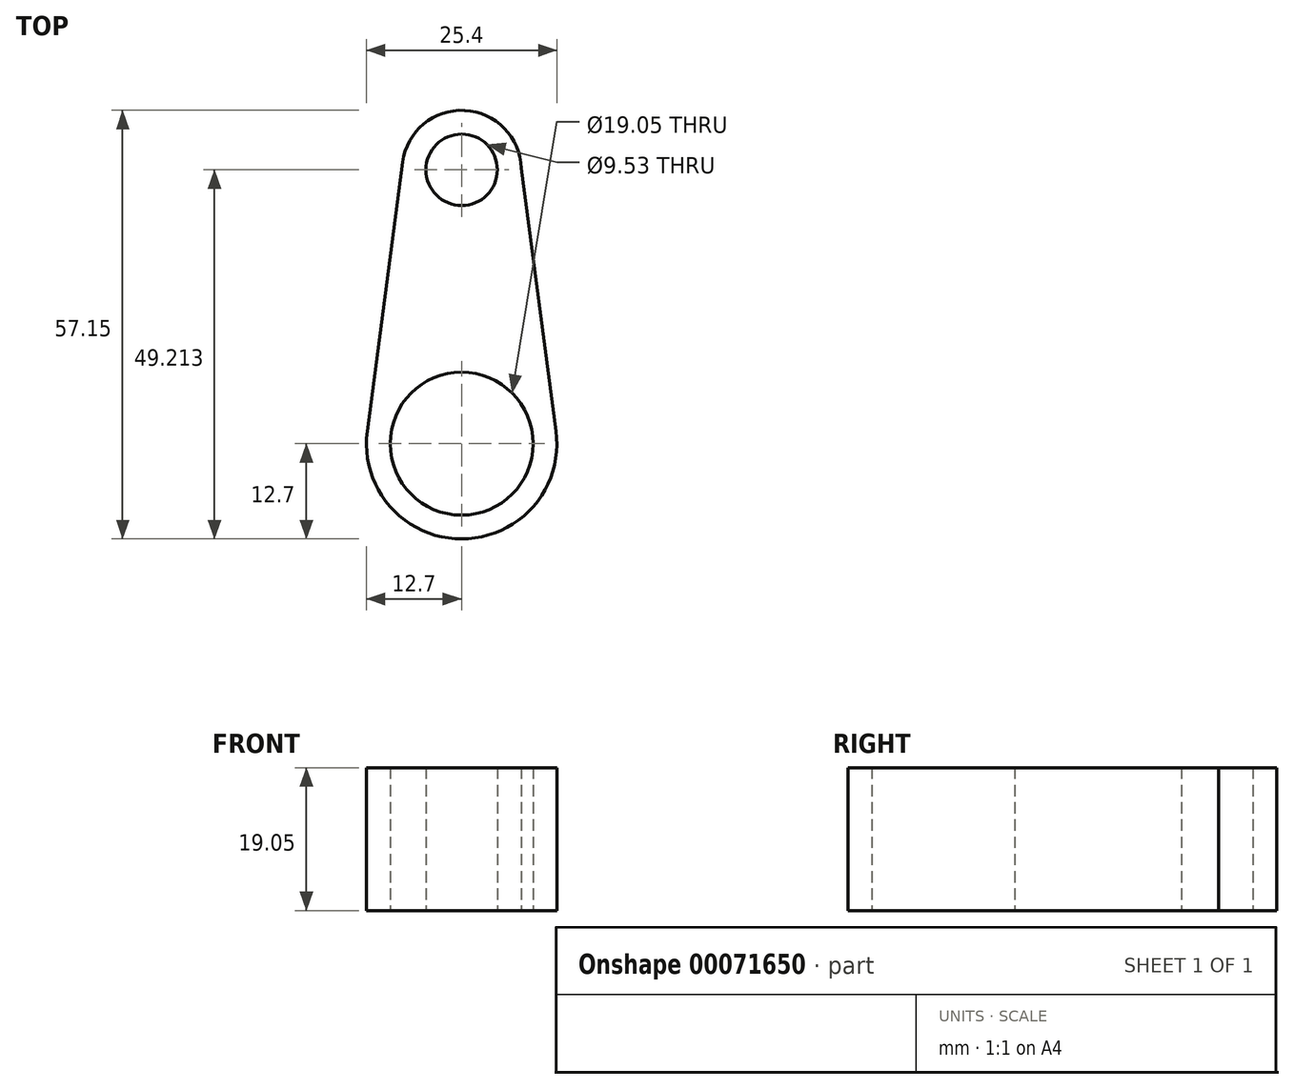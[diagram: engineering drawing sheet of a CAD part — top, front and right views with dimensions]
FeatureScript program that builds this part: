
annotation { "Feature Type Name" : "Feature", "Feature Type Description" : "" }
export const myFeature = defineFeature(function(context is Context, id is Id, definition is map)
    precondition{}
    {
        {
            var Q0;
            Q0=qCreatedBy(makeId("Top.planeOp"),FACE);
            var sketch = newSketch(context, id + "F0", { "sketchPlane" : qUnion([Q0])});
            skCircle(sketch, "E0", {"center": v(0, 0) * mm, "radius": 12.7 * mm});
            skCircle(sketch, "E1", {"center": v(0, 0) * mm, "radius": 9.53 * mm});
            skCircle(sketch, "E2", {"center": v(0, 36.51) * mm, "radius": 7.94 * mm});
            skCircle(sketch, "E3", {"center": v(0, 36.51) * mm, "radius": 4.76 * mm});
            skLineSegment(sketch, "E4", {"start": v(-7.87, 37.55) * mm, "end": v(-12.6, 1.66) * mm});
            skLineSegment(sketch, "E5", {"start": v(7.93, 36.73) * mm, "end": v(12.59, 1.67) * mm});
            skSolve(sketch);
        }
        {
            var Q0;
            Q0=makeQuery(id+"F0.imprint","IMPRINT",FACE,{"disambiguationData":[TD([[makeQuery(id+"F0.imprint","IMPRINT",EDGE,{"derivedFrom":sQuery(id+"F0.wireOp",EDGE,"E1")}),-1.0]])]});
            var Q1;
            {var subQ0=sQuery(id+"F0.wireOp",EDGE,"E4");Q1=makeQuery(id+"F0.imprint","IMPRINT",FACE,{"disambiguationData":[TD([[makeQuery(id+"F0.imprint","IMPRINT",EDGE,{"derivedFrom":subQ0}),1.0]])]});}
            var Q2;
            Q2=makeQuery(id+"F0.imprint","IMPRINT",FACE,{"disambiguationData":[TD([[makeQuery(id+"F0.imprint","IMPRINT",EDGE,{"derivedFrom":sQuery(id+"F0.wireOp",EDGE,"E3")}),-1.0]])]});
            extrude(context, id + "F1", {"entities" : qUnion([Q0, Q1, Q2]), "depth" : 19.05 * mm});
        }
    });
